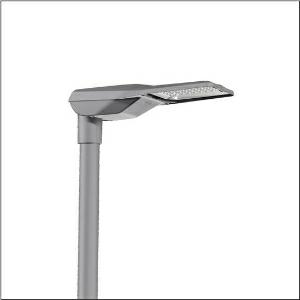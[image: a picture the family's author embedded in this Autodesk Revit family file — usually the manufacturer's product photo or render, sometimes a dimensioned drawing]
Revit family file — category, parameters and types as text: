
# Revit family: streetlight_sl_21_iq_mini___st1_0a_5xe2d31d08hb_45ae
name_source: partatom
category: Lighting Fixtures
units: mm (PartAtom-declared; Revit-internal decimal feet)

## family parameters
Cut with Voids When Loaded = No
Host = Face
Light Source = No
Part Type = Normal
Room Calculation Point = No
Round Connector Dimension = Use Diameter
Shared = No

## types (1)
- --- (1 x LED, 9450 lm, 70.9 W, 3000K)
    Apparent Load = 71 VA
    CIE Flux Codes = 37 72 97 100 100
    Color Rendering = 70
    Color Temperature = 3000K
    Default Elevation = 1800 mm
    Description = Streetlight SL 21 iQ mini, mast luminaire, primary light control with lens, of PMMA, primary optical cover: cover, of toughened safety glass, transparent, light distribution: ST1.0a, light emission: direct distribution, primary light characteristic: asymmetric, installation type: post-top, side-entry, LED, High Power LED, rated luminous flux: 9.450lm, luminous efficacy: 133lm/W, light colour: 730, colour temperature: 3000K, control gear: iQ-Comfort, control: Auto-Match, Temp-Guard, Lumen-Switch, Night-Set, Smart-Wire, Light-Fading, Desk-Remote (wireless, voltage-free reading and setting of iQ features in the workshop via application-optimized NFC function/RFID function), optimised constant luminous flux control (CLO 2.0), pre-setting: linear dimming characteristic, mains connection: 220..240V, AC, 50/60Hz, start of lifetime: 71W, end of service life: 75W, reduction: 31W, luminaire housing, of diecast aluminium, powder-coated, Siteco® metallic grey (DB 702S), corrosivity category C5 mid according to DIN EN ISO 12944, please order mast flange separately, inclination adjustable: 0°, 5°, 10°, 15°, sealing non-destructively replaceable, multi-level sealing system, length: 628mm, width: 235mm, height: 110mm, mast flange for spigot size: 42mm (side-entry): 5XC10008XM4, 60/48mm (side-entry/post-top): 5XC10108XM2, 76/60mm (side-entry/post-top): 5XC10108XM1, mounting height: 4..8m, protection rating (complete): IP66, insulation class (complete): insulation class II (safety insulation), certification: CE, ENEC, ENEC+, VDE, impact resistance: IK10, permissible operating ambient temperature for outdoor applications: -40..+50°C, standard-compliant lighting for roads and squares, packaging unit: 1 piece

Light Distribution: ST1.0a
    Height = 110 mm
    Lamp = 1 x LED
    Lamp Light Flux = 9450 lm
    Lamp Power = 70.9 W
    Lamp count = 1
    Length = 625 mm
    Luminous efficacy = 133 lm/W
    Manufacturer = Siteco
    ModVariant = No
    Model = 5XE2D31D08HB
    Number of Poles = 1
    OnlyDefault = Yes
    Power Factor = 1
    Product Name = Streetlight SL 21 iQ mini | ST1.0a
    Product group = mast luminaire | pylon top
    ProductGroupID = 6100
    Protection Class = Protection class II
    Protection Degree = IP 66
    RLX_Detail_Level = 1
    RLX_Emergency_Light_Flux = 0 lm
    RLX_Emergency_Type = 0
    RLX_Emergency_Type_DB = No
    RlxData = <blob elided: 26285 chars, md5=c296a838>
    Socket = socket
    Standby Power = 0 W
    System Light Flux = 9450 lm
    System Power = 71 W
    Type Comments = factory setting: luminous flux: 100 % | dim-lin: 254 | 711 mA
    Type Image = l_1003519.jpg
    URL = http://relux.com
    VarID = @adj_158188
    Voltage = 0 V
    Weight = 0.00 kg
    Width = 234 mm

## geometry (parser evidence)
native form markers: Blend x4, Sweep x10
no freeform markers — native parametric forms only
